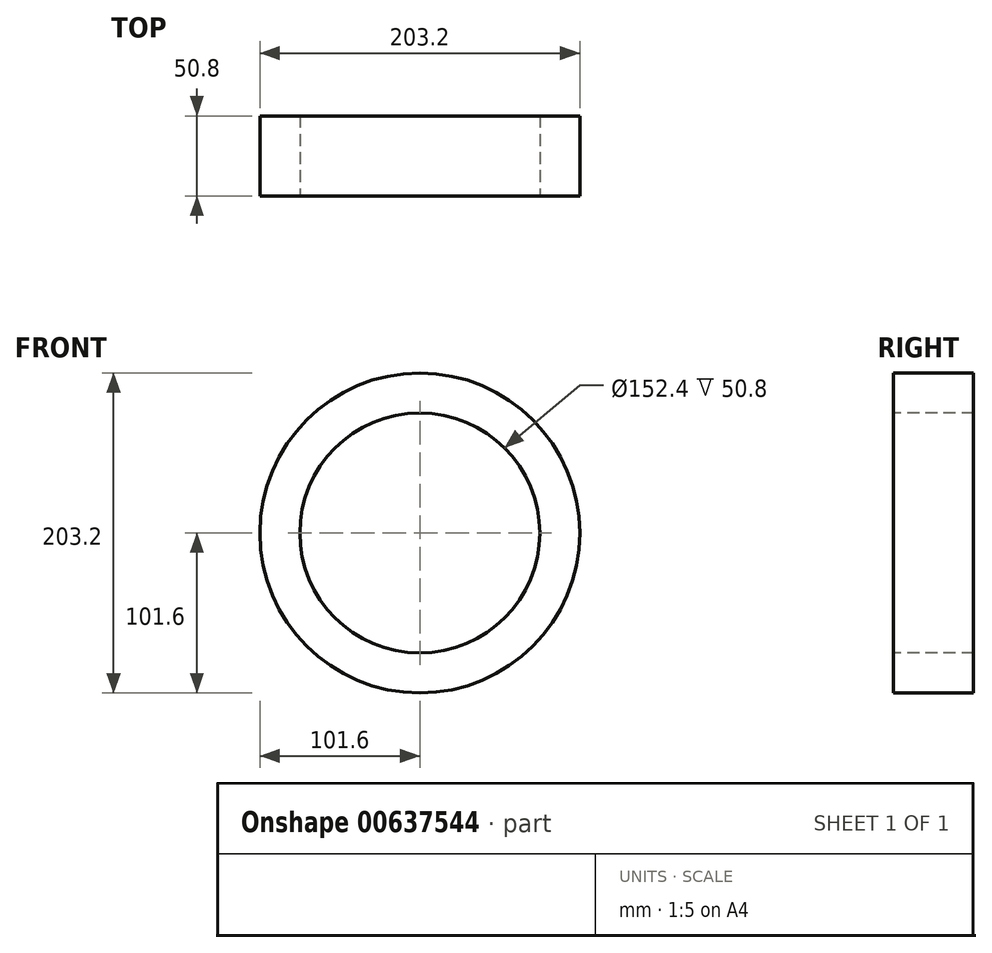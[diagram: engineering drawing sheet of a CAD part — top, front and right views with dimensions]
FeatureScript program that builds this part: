
annotation { "Feature Type Name" : "Feature", "Feature Type Description" : "" }
export const myFeature = defineFeature(function(context is Context, id is Id, definition is map)
    precondition{}
    {
        {
            var Q0;
            Q0=qCreatedBy(makeId("Top.planeOp"),FACE);
            var sketch = newSketch(context, id + "F0", { "sketchPlane" : qUnion([Q0])});
            skLineSegment(sketch, "E0.bottom", {"start": v(76.2, 0) * mm, "end": v(101.6, 0) * mm});
            skLineSegment(sketch, "E0.top", {"start": v(76.2, 50.8) * mm, "end": v(101.6, 50.8) * mm});
            skLineSegment(sketch, "E0.left", {"start": v(76.2, 0) * mm, "end": v(76.2, 50.8) * mm});
            skLineSegment(sketch, "E0.right", {"start": v(101.6, 0) * mm, "end": v(101.6, 50.8) * mm});
            skLineSegment(sketch, "E1", {"start": v(0, 0) * mm, "end": v(0, 117.9) * mm, "construction": true});
            skSolve(sketch);
        }
        {
            var Q0;
            Q0=makeQuery(id+"F0.imprint","IMPRINT",FACE,{"disambiguationData":[TD([[makeQuery(id+"F0.imprint","IMPRINT",EDGE,{"derivedFrom":sQuery(id+"F0.wireOp",EDGE,"E0.bottom")}),1.0]])]});
            var Q1;
            Q1=sQuery(id+"F0.wireOp",EDGE,"E1");
            revolve(context, id + "F1", {"entities" : qUnion([Q0]), "axis" : qUnion([Q1]), "revolveType" : RevolveType.FULL});
        }
    });
